# Revit family: Washer_Milnor_30022-V8Z
name_source: partatom
category: Mechanical Equipment
units: mm (PartAtom-declared; Revit-internal decimal feet)

## family parameters
Always vertical = No
Classification Number = 23.45.70.11.14.11
Cut with Voids When Loaded = No
Maintain Annotation Orientation = No
Part Type = Normal
Room Calculation Point = No
Round Connector Dimension = Use Diameter
Shared = No
Work Plane-Based = Yes

## types (9) — shared parameters
Assembly Code = E1010610
Capacity = 60 lbs Dry Weight
Cylinder Depth = 1' - 10"
Cylinder Diameter = 2' - 6"
Cylinder Volume = 9 CF
Default Elevation = 4' - 0"
Description = Milnor Commercial Washer Extractor - Model 30022 V8Z as Specified
Door Base from FF = 2' - 3 3/16"
Door Opening = 1' - 3 1/2"
Door Opening Depth = 2' - 3 5/16"
Dynamic Load = 3810.00 kip
Keynote = 11110
Manufacturer = Pellerin Milnor Corp
Manufacturer Fax = 504-468-3094
Manufacturer Website = http://www.milnor.com
Model = 30022 V8Z
Number of Poles = 1
Product Data = http://www.arcat.com
Revision = R1_04-2011
Sales Information = http://www.milnor.com
Send Message = http://www.arcat.com
URL = http://www.milnor.com
Unit Depth = 4' - 8 1/2"
Unit Height = 4' - 10 11/16"
Unit Weight = 1344
Unit Width = 2' - 10 1/2"
Vibration Frequency = 14
doorgas = 1' - 6"
zero-valued in all types: Expected Lifespan (Years), Maintenance Schedule (Months), Warranty Duration (Years)

## per-type parameters (varying)
| type | Frequency | MEP Amperage | Phase | Voltage_MEP |
| MilTouch 415-50-3ph | 50 Hz | 5 A | 3 | 415 V |
| MilTouch 380-50-3ph | 50 Hz | 5 A | 3 | 380 V |
| MilTouch 220-50-3ph | 50 Hz | 7 A | 3 | 220 V |
| MilTouch 480-60-3ph | 60 Hz | 4 A | 3 | 480 V |
| MilTouch 380-60-3ph | 60 Hz | 5 A | 3 | 380 V |
| MilTouch 240-60-3ph | 60 Hz | 7 A | 3 | 240 V |
| MilTouch 208-60-3ph | 60 Hz | 8 A | 3 | 208 V |
| MilTouch 240-60-1ph | 60 Hz | 8 A | 1 | 240 V |
| MilTouch 208-60-1ph | 60 Hz | 9 A | 1 | 208 V |

## geometry (parser evidence)
native form markers: Sweep x2
no freeform markers — native parametric forms only
